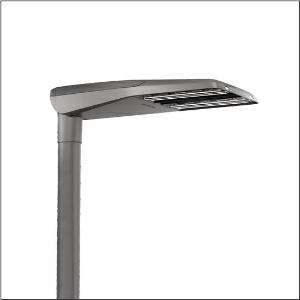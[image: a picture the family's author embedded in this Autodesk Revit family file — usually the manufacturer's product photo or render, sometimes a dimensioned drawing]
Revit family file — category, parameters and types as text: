
# Revit family: streetlight_sl_11_iq_midi___st1_0p1_0_5xc3k51f08me_0ac4
name_source: partatom
category: Lighting Fixtures
units: mm (PartAtom-declared; Revit-internal decimal feet)

## family parameters
Cut with Voids When Loaded = No
Host = Face
Light Source = No
Part Type = Normal
Room Calculation Point = No
Round Connector Dimension = Use Diameter
Shared = No

## types (1)
- --- (1 x LED, 17550 lm, 124.7 W, 3000K)
    Apparent Load = 125 VA
    CIE Flux Codes = 32 65 95 100 100
    Color Rendering = 70
    Color Temperature = 3000K
    Default Elevation = 1800 mm
    Description = Streetlight SL 11 iQ midi, mast luminaire, primary light control with 3 zone facetted reflector, of plastic, silver coated, highly specular, primary optical cover: cover, of PMMA, transparent, light distribution: ST1.0P1.0, light emission: direct distribution, primary light characteristic: asymmetric, installation type: post-top, side-entry, LED, High Power LED, rated luminous flux: 17.550lm, luminous efficacy: 141lm/W, light colour: 730, colour temperature: 3000K, control: Street-Remote, Auto-Match, Temp-Guard, Lumen-Switch, Night-Set, Smart-Wire, Light-Fading, Desk-Remote (wireless, voltage-free reading and setting of iQ features in the workshop via application-optimized NFC function/RFID function), optimised constant luminous flux control (CLO 2.0), with cable H07RN-F 5x 1.5mm², mains connection: 230..240V, AC, 50/60Hz, connection cable pre-assembled, cable length: 12,5m, start of lifetime: 125W, end of service life: 132W, reduction: 57W, luminaire housing, of diecast aluminium, powder-coated, Siteco® metallic grey (DB 702S), please order mast flange separately, inclination adjustable without tools: 0°, 5°, 10°, 15° (post-top) | 0°, -5°, -10°, -15° (side-entry), sealing non-destructively replaceable, multi-level sealing system, length: 780mm, width: 376mm, height: 118mm, mast flange for spigot size: 42mm (side-entry): 5XC10008XM4, 60/48mm (side-entry/post-top): 5XC10108XM2, 76/60mm (side-entry/post-top): 5XC10108XM1, equipment: Power, protection rating (complete): IP66, insulation class (complete): insulation class II (safety insulation), certification: CE, ENEC, VDE, impact resistance: IK09, permissible operating ambient temperature for outdoor applications: -25..+50°C, standard-compliant lighting for roads and squares, Environmental Product Declaration (EPD) tested and certified by an independent institute, packaging unit: 1 piece

Light Distribution: ST1.0P1.0
    Height = 118 mm
    Lamp = 1 x LED
    Lamp Light Flux = 17550 lm
    Lamp Power = 124.7 W
    Lamp count = 1
    Length = 780 mm
    Luminous efficacy = 141 lm/W
    Manufacturer = Siteco
    ModVariant = No
    Model = 5XC3K51F08ME
    Number of Poles = 1
    OnlyDefault = Yes
    Power Factor = 1
    Product Name = Streetlight SL 11 iQ midi | ST1.0P1.0
    Product group = mast luminaire | pylon top
    ProductGroupID = 6100
    Protection Class = Protection class II
    Protection Degree = IP 66
    RLX_Detail_Level = 1
    RLX_Emergency_Light_Flux = 0 lm
    RLX_Emergency_Type = 0
    RLX_Emergency_Type_DB = No
    RlxData = <blob elided: 70709 chars, md5=beeafbb4>
    Socket = socket
    Standby Power = 0 W
    System Light Flux = 17550 lm
    System Power = 125 W
    Type Comments = factory setting: luminous flux: 100 % | dim-lin: 254 | 557 mA
    Type Image = l_1005960.jpg
    URL = http://relux.com
    VarID = @adj_003333
    Voltage = 0 V
    Weight = 0.00 kg
    Width = 376 mm

## geometry (parser evidence)
native form markers: Blend x4, Sweep x8
no freeform markers — native parametric forms only
